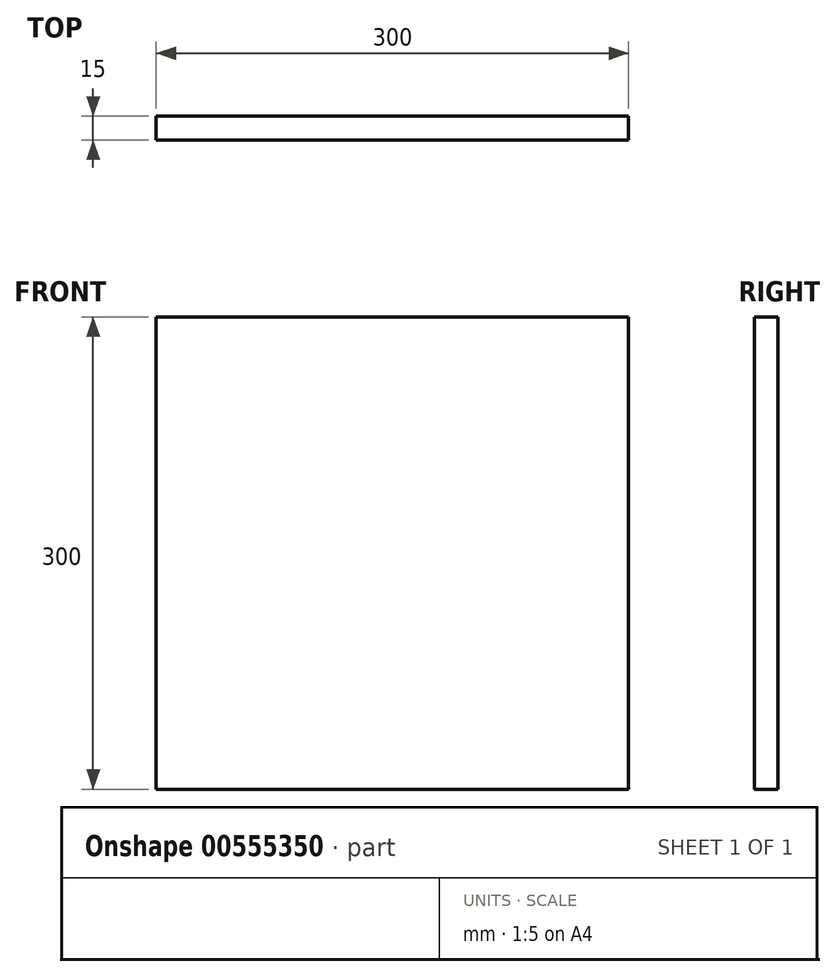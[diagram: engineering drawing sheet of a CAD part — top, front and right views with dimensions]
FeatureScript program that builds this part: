
annotation { "Feature Type Name" : "Feature", "Feature Type Description" : "" }
export const myFeature = defineFeature(function(context is Context, id is Id, definition is map)
    precondition{}
    {
        {
            var Q0;
            Q0=qCreatedBy(makeId("Front.planeOp"),FACE);
            var sketch = newSketch(context, id + "F0", { "sketchPlane" : qUnion([Q0])});
            skLineSegment(sketch, "E0", {"start": v(-116.15, 67.2) * mm, "end": v(183.85, 67.2) * mm});
            skLineSegment(sketch, "E1", {"start": v(183.85, 67.2) * mm, "end": v(183.85, -232.8) * mm});
            skLineSegment(sketch, "E2", {"start": v(183.85, -232.8) * mm, "end": v(-116.15, -232.8) * mm});
            skLineSegment(sketch, "E3", {"start": v(-116.15, -232.8) * mm, "end": v(-116.15, 67.2) * mm});
            skSolve(sketch);
        }
        {
            var Q0;
            Q0=makeQuery(id+"F0.imprint","IMPRINT",FACE,{"disambiguationData":[TD([[makeQuery(id+"F0.imprint","IMPRINT",EDGE,{"derivedFrom":sQuery(id+"F0.wireOp",EDGE,"E0")}),-1.0]])]});
            extrude(context, id + "F1", {"entities" : qUnion([Q0]), "depth" : 15 * mm, "offsetDistance" : 25 * mm});
        }
    });
